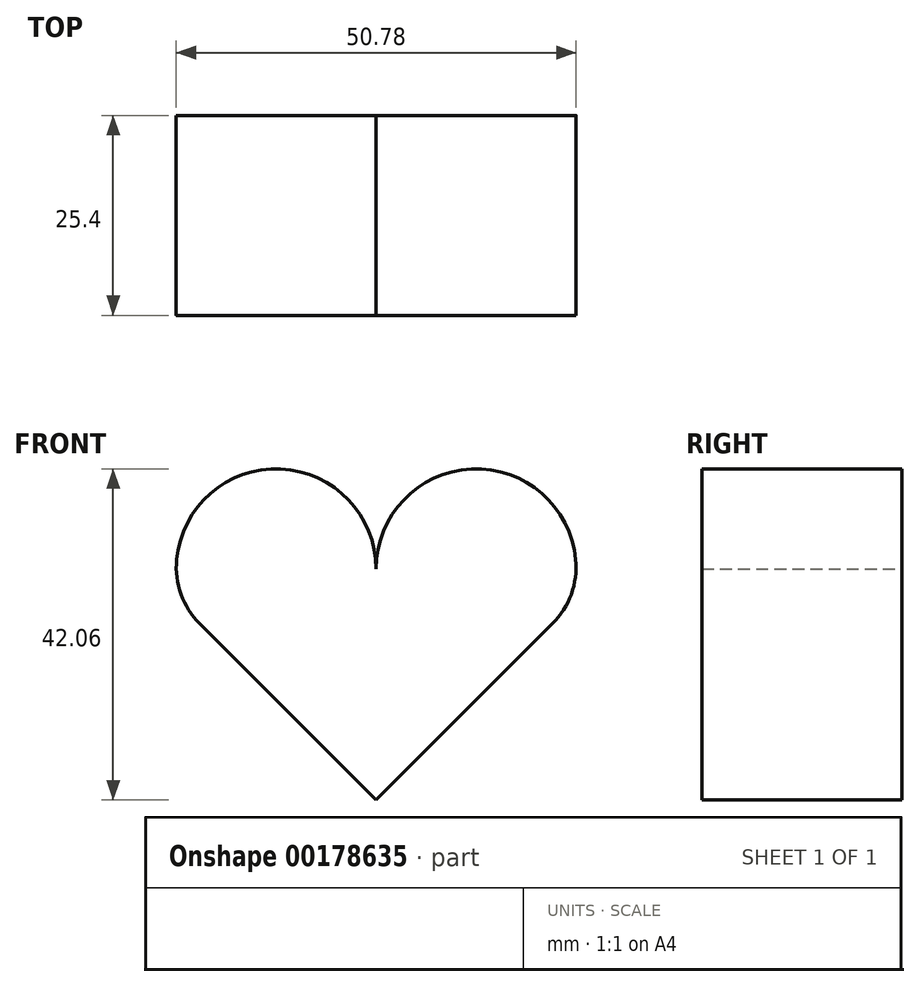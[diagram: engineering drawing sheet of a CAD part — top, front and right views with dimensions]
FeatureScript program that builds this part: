
annotation { "Feature Type Name" : "Feature", "Feature Type Description" : "" }
export const myFeature = defineFeature(function(context is Context, id is Id, definition is map)
    precondition{}
    {
        {
            var Q0;
            Q0=qCreatedBy(makeId("Front.planeOp"),FACE);
            var sketch = newSketch(context, id + "F0", { "sketchPlane" : qUnion([Q0])});
            skLineSegment(sketch, "E0", {"start": v(0, -24.38) * mm, "end": v(-22.41, -1.97) * mm});
            skLineSegment(sketch, "E1", {"start": v(0, -24.38) * mm, "end": v(22.41, -1.97) * mm});
            skArc(sketch, "E2", {"start": v(0, 4.98) * mm, "mid": v(-12.11, 17.67) * mm, "end": v(-25.35, 6.15) * mm});
            skArc(sketch, "E3", {"start": v(25.35, 6.15) * mm, "mid": v(12.11, 17.67) * mm, "end": v(0, 4.98) * mm});
            skPoint(sketch, "E4.visualSharp", {"position": v(-24.38, 0) * mm});
            skArc(sketch, "E4.filletArc", {"start": v(-25.35, 6.15) * mm, "mid": v(-24.79, 1.76) * mm, "end": v(-22.41, -1.97) * mm});
            skPoint(sketch, "E5.visualSharp", {"position": v(24.38, 0) * mm});
            skArc(sketch, "E5.filletArc", {"start": v(22.41, -1.97) * mm, "mid": v(24.79, 1.76) * mm, "end": v(25.35, 6.15) * mm});
            skSolve(sketch);
        }
        {
            var Q0;
            Q0 = qSketchRegion(id + "F0", true);
            extrude(context, id + "F1", {"entities" : qUnion([Q0]), "depth" : 25.4 * mm});
        }
    });
